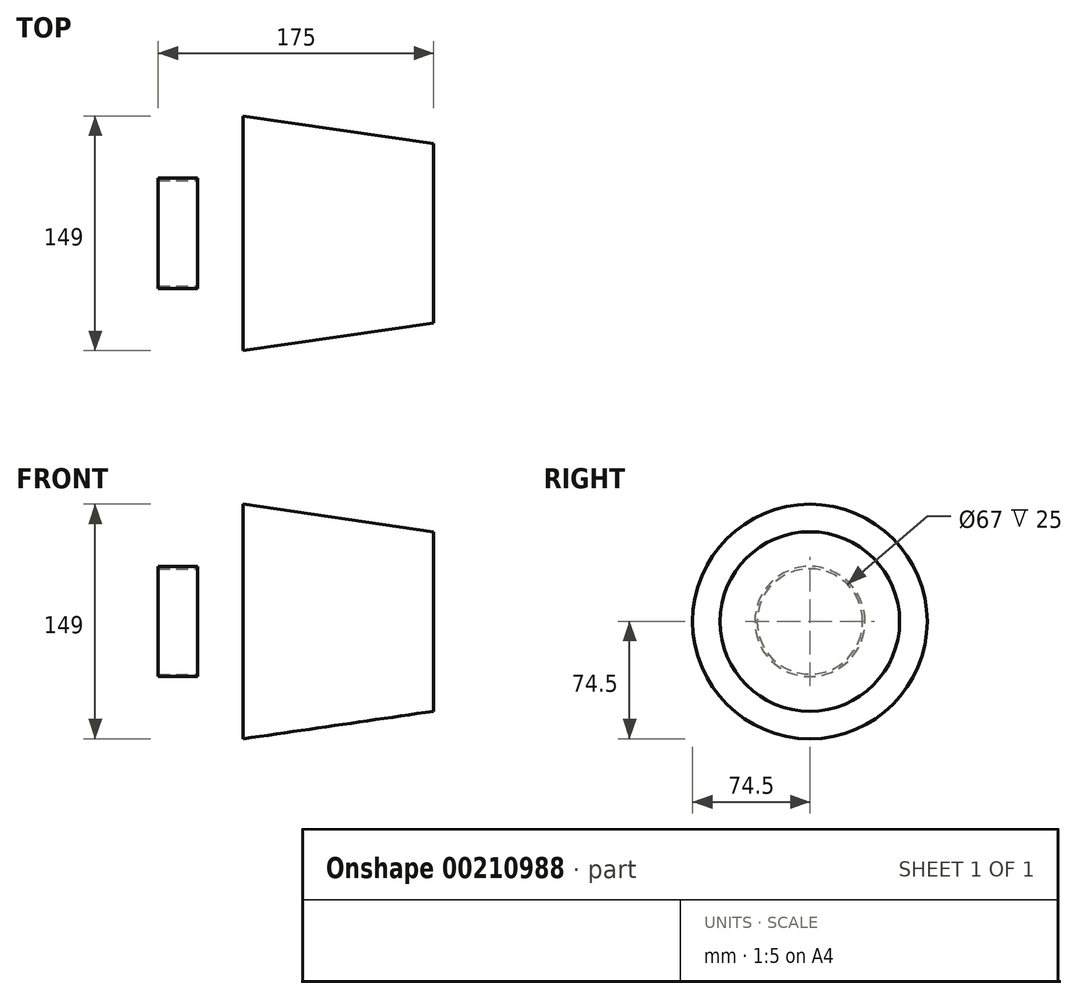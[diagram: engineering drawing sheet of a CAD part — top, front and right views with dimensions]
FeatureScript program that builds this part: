
annotation { "Feature Type Name" : "Feature", "Feature Type Description" : "" }
export const myFeature = defineFeature(function(context is Context, id is Id, definition is map)
    precondition{}
    {
        {
            var Q0;
            Q0=qCreatedBy(makeId("Right.planeOp"),FACE);
            var sketch = newSketch(context, id + "F0", { "sketchPlane" : qUnion([Q0])});
            skCircle(sketch, "E0", {"center": v(0, 0) * mm, "radius": 57 * mm});
            skSolve(sketch);
        }
        {
            var Q0;
            Q0=qCreatedBy(makeId("Right.planeOp"),FACE);
            cPlane(context, id + "F1", {"entities" : qUnion([Q0]), "cplaneType" : CPlaneType.OFFSET, "offset" : 121 * mm, "oppositeDirection" : true, "width" : 150 * mm, "height" : 150 * mm});
        }
        {
            var Q0;
            Q0=qCreatedBy(id+"F1.planeOp",FACE);
            var sketch = newSketch(context, id + "F2", { "sketchPlane" : qUnion([Q0])});
            skCircle(sketch, "E1", {"center": v(0, 0) * mm, "radius": 74.5 * mm});
            skSolve(sketch);
        }
        {
            var Q0;
            Q0=qCreatedBy(makeId("Right.planeOp"),FACE);
            cPlane(context, id + "F3", {"entities" : qUnion([Q0]), "cplaneType" : CPlaneType.OFFSET, "offset" : 175 * mm, "oppositeDirection" : true, "width" : 150 * mm, "height" : 150 * mm});
        }
        {
            var Q0;
            Q0=qCreatedBy(makeId("Right.planeOp"),FACE);
            cPlane(context, id + "F4", {"entities" : qUnion([Q0]), "cplaneType" : CPlaneType.OFFSET, "offset" : 150 * mm, "oppositeDirection" : true, "width" : 150 * mm, "height" : 150 * mm});
        }
        {
            var Q0;
            Q0=qCreatedBy(id+"F4.planeOp",FACE);
            var sketch = newSketch(context, id + "F5", { "sketchPlane" : qUnion([Q0])});
            skCircle(sketch, "E2", {"center": v(0, 0) * mm, "radius": 35 * mm});
            skCircle(sketch, "E3", {"center": v(0, 0) * mm, "radius": 33.5 * mm});
            skSolve(sketch);
        }
        {
            var Q0;
            Q0=makeQuery(id+"F5.imprint","IMPRINT",FACE,{"disambiguationData":[TD([[makeQuery(id+"F5.imprint","IMPRINT",EDGE,{"derivedFrom":sQuery(id+"F5.wireOp",EDGE,"E2")}),1.0]])]});
            var Q1;
            Q1=sQuery(id+"F5.wireOp",EDGE,"E3");
            var Q2;
            Q2=sQuery(id+"F5.wireOp",EDGE,"E2");
            var Q3;
            Q3=qCreatedBy(id+"F3.planeOp",FACE);
            extrude(context, id + "F6", {"entities" : qUnion([Q0]), "surfaceEntities" : qUnion([Q1, Q2]), "endBound" : BoundingType.UP_TO_SURFACE, "oppositeDirection" : true, "depth" : 18 * mm, "endBoundEntityFace" : qUnion([Q3]), "offsetDistance" : 25 * mm});
        }
        {
            var Q0;
            Q0=makeQuery(id+"F0.imprint","IMPRINT",FACE,{"disambiguationData":[TD([[makeQuery(id+"F0.imprint","IMPRINT",EDGE,{"derivedFrom":sQuery(id+"F0.wireOp",EDGE,"E0")}),1.0]])]});
            var Q1;
            Q1=makeQuery(id+"F2.imprint","IMPRINT",FACE,{"disambiguationData":[TD([[makeQuery(id+"F2.imprint","IMPRINT",EDGE,{"derivedFrom":sQuery(id+"F2.wireOp",EDGE,"E1")}),1.0]])]});
            loft(context, id + "F7", {"sheetProfilesArray" : [{ "sheetProfileEntities" : qUnion([Q0]) }, { "sheetProfileEntities" : qUnion([Q1]) }]});
        }
    });
